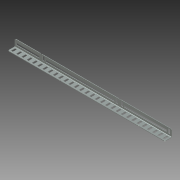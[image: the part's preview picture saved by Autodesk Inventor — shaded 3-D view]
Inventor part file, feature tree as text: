
AUTODESK INVENTOR PART (.ipt)
format: ipt  version: 2013 (Build 170138000, 138)  size: 679,424 bytes
history: native  units: mm (DEFAULTED — no unit token found)
features: other x79, extrude x75, sketch x8, sheet_metal_op x3, pattern_linear x1
ambient origin geometry x8: Origin, YZ Plane, XZ Plane, XY Plane, X Axis, Y Axis, Z Axis, Center Point
bodies: Solid1 (feature_tree)
feature tree (166):
  sheet_metal_op  "Face1"
  sheet_metal_op  "Flange1"
  other  "Corner Chamfer1"
  extrude  "Extrusion1"  Depth=9.779mm
  pattern_linear  "Rectangular Pattern1"  Count1=30 Spacing1=12.7mm
  sketch  "Sketch8"  dims[d25=4.064mm d26=1.905mm d27=1.905mm d28=1.905mm d29=1.905mm d30=1.27mm d31=1.27mm d32=0.635mm d33=2.54mm d34=1.27mm d35=16.51mm d36=90.0deg d37=0.8636mm d38=1.905mm d39=6.35mm d40=45.0deg d41=3.302mm d42=4.064mm d43=4.572mm d45=1.905mm d46=1.905mm d47=0.0mm d48=4.064mm d49=4.572mm d50=3.429mm d51=9.779mm d52=3.048mm d53=4.572mm d54=177.8mm d55=3.048mm d56=4.572mm d58=1.905mm d59=1.905mm d60=0.0mm d61=4.064mm d62=4.064mm d63=4.572mm d64=3.048mm d65=4.064mm d67=3.048mm d68=4.572mm d69=1.27mm d70=0.0mm d71=0.508mm d72=0.508mm d73=13.208mm d74=3.81mm d75=3.048mm d76=0.0mm d77=0.508mm d78=0.508mm d79=3.81mm d80=13.208mm d81=3.302mm d82=25.4mm d83=0.0mm d84=25.4mm d85=0.0mm d86=300.0mm d88=12.7mm d89=0.0mm d90=0.0mm d91=0.0mm d92=0.0mm d93=0.0mm d94=0.0mm d95=0.0mm d96=0.0mm d97=0.0mm d98=0.0mm d99=0.0mm d100=0.0mm d101=0.0mm d102=0.0mm d103=0.0mm d104=0.0mm d105=0.0mm d106=0.0mm d107=0.0mm d108=0.0mm d109=0.0mm d110=0.0mm d111=0.0mm d112=0.0mm d113=0.0mm d114=0.0mm d115=0.0mm d116=0.0mm d117=0.0mm d118=0.0mm d119=0.0mm d120=0.0mm d121=0.0mm d122=0.0mm d123=0.0mm d124=0.0mm d125=0.0mm d126=0.0mm d127=0.0mm d128=0.0mm d129=0.0mm d130=0.0mm d131=0.0mm d132=0.0mm d133=0.0mm d134=0.0mm d135=0.0mm d136=0.0mm d137=0.0mm d138=0.0mm d139=0.0mm d140=0.0mm d141=0.0mm d142=0.0mm d143=0.0mm d144=0.0mm d145=0.0mm d146=0.0mm d147=0.0mm d148=0.0mm d149=0.0mm d150=0.0mm d151=0.0mm d152=0.0mm d153=0.0mm d154=0.0mm d155=0.0mm d156=0.0mm d157=0.0mm d158=0.0mm d159=0.0mm d160=0.0mm d161=0.0mm d162=0.0mm d163=0.0mm d164=0.0mm d165=0.0mm d166=0.0mm d167=0.0mm d168=0.0mm d169=0.0mm d170=0.0mm d171=0.0mm d172=0.0mm d173=0.0mm d174=0.0mm d175=0.0mm d176=0.0mm d177=0.0mm d178=0.0mm d179=0.0mm d180=0.0mm d181=0.0mm d182=0.0mm d183=0.0mm d184=0.0mm d185=0.0mm d186=0.0mm d187=0.0mm d188=0.0mm d189=0.0mm d190=0.0mm d191=0.0mm d192=0.0mm d193=0.0mm d194=0.0mm d195=0.0mm d196=0.0mm d197=0.0mm d198=0.0mm d199=0.0mm d200=0.0mm d201=0.0mm d202=0.0mm d229=1.27mm d230=0.0mm d231=127.0mm d232=1.905mm d233=1.905mm d234=63.179403mm d235=1.905mm d236=1.905mm d237=25.4mm d238=0.0mm d239=25.4mm d240=0.0mm d241=25.4mm d242=0.0mm d243=25.4mm d244=0.0mm d245=25.4mm d246=0.0mm d247=25.4mm d248=0.0mm d249=25.4mm d250=0.0mm d251=25.4mm d252=0.0mm d253=25.4mm d254=0.0mm d255=25.4mm d256=0.0mm d257=25.4mm d258=0.0mm d259=25.4mm d260=0.0mm d261=25.4mm d262=0.0mm d263=25.4mm d264=0.0mm d265=0.0mm d266=0.0mm d267=0.0mm d268=0.0mm d269=0.0mm d270=0.0mm d271=0.0mm d272=0.0mm d273=0.0mm d274=0.0mm d275=0.0mm d276=0.0mm d277=0.0mm d278=0.0mm d279=0.0mm d280=0.0mm d281=0.0mm d282=0.0mm d283=0.0mm d284=0.0mm d285=0.0mm d286=0.0mm d287=0.0mm d288=0.0mm d289=0.0mm d290=0.0mm d291=0.0mm d292=0.0mm]
  sketch  "Sketch1"  dims[d1=4.064mm d2=9.779mm]
  other  "Plate1"
  sketch  "Sketch2"  dims[d3=4.572mm]
  other  "Plate2"
  sheet_metal_op  "Bend1"
  sketch  "Sketch3"  dims[d12=16.51mm]
  sketch  "Sketch4"  dims[d14=1.905mm]
  sketch  "Sketch5"  dims[d15=1.905mm]
  other  "Srf1"
  sketch  "Sketch6"  dims[d16=1.905mm]
  other  "Srf2"
  other  "Srf4"
  other  "Srf6"
  other  "Srf8"
  other  "Srf10"
  other  "Srf12"
  other  "Srf14"
  other  "Srf16"
  other  "Srf18"
  other  "Srf20"
  other  "Srf22"
  other  "Srf24"
  other  "Srf26"
  other  "Srf28"
  other  "Srf30"
  other  "Srf32"
  other  "Srf34"
  other  "Srf36"
  other  "Srf38"
  other  "Srf40"
  other  "Srf42"
  other  "Srf44"
  other  "Srf46"
  other  "Srf48"
  other  "Srf50"
  other  "Srf52"
  other  "Srf54"
  other  "Srf56"
  other  "Srf58"
  other  "Srf60"
  other  "Srf3"
  other  "Srf5"
  other  "Srf7"
  other  "Srf9"
  other  "Srf11"
  other  "Srf13"
  other  "Srf15"
  other  "Srf17"
  other  "Srf19"
  other  "Srf21"
  other  "Srf23"
  other  "Srf25"
  other  "Srf27"
  other  "Srf29"
  other  "Srf31"
  other  "Srf33"
  other  "Srf35"
  other  "Srf37"
  other  "Srf39"
  other  "Srf41"
  other  "Srf43"
  other  "Srf45"
  other  "Srf47"
  other  "Srf49"
  other  "Srf51"
  other  "Srf53"
  other  "Srf55"
  other  "Srf57"
  other  "Srf59"
  sketch  "Sketch7"  dims[d17=1.905mm d18=300.0mm d20=12.7mm d21=10.0mm d23=25.4mm]
  other  "Srf61"
  other  "Srf62"
  other  "Srf63"
  other  "Srf64"
  other  "Srf65"
  other  "Srf66"
  other  "Srf67"
  other  "Srf68"
  other  "Srf69"
  other  "Srf70"
  other  "Srf71"
  other  "Srf72"
  other  "Srf73"
  other  "Srf74"
  other  "Cut1"
  extrude  "ExtrusionSrf1"  Depth=1.905mm
  extrude  "ExtrusionSrf2"  Depth=1.905mm
  other  "Cut2"
  extrude  "ExtrusionSrf61"  Depth=1.905mm
  extrude  "ExtrusionSrf62"  Depth=1.905mm
  extrude  "ExtrusionSrf63"  Depth=1.27mm
  extrude  "ExtrusionSrf64"  Depth=1.27mm
  extrude  "ExtrusionSrf65"  Depth=0.635mm
  extrude  "ExtrusionSrf66"  Depth=2.54mm
  extrude  "ExtrusionSrf67"  Depth=1.27mm
  extrude  "ExtrusionSrf68"  Depth=16.51mm TaperAngle=90.0deg
  extrude  "ExtrusionSrf69"  Depth=1.905mm TaperAngle=45.0deg
  extrude  "ExtrusionSrf70"  Depth=3.302mm
  extrude  "ExtrusionSrf71"  Depth=4.064mm
  extrude  "ExtrusionSrf72"  Depth=4.572mm
  extrude  "ExtrusionSrf73"  Depth=1.905mm
  extrude  "ExtrusionSrf74"  Depth=1.905mm
  extrude  "ExtrusionSrf3"  TaperAngle=0.0deg  [1 undecoded]
  extrude  "ExtrusionSrf4"  Depth=4.064mm
  extrude  "ExtrusionSrf5"  Depth=4.572mm
  extrude  "ExtrusionSrf6"  Depth=3.429mm
  extrude  "ExtrusionSrf7"  Depth=9.779mm
  extrude  "ExtrusionSrf8"  Depth=3.048mm
  extrude  "ExtrusionSrf9"  Depth=4.572mm
  extrude  "ExtrusionSrf10"  Depth=177.8mm
  extrude  "ExtrusionSrf11"  Depth=3.048mm
  extrude  "ExtrusionSrf12"  Depth=4.572mm
  extrude  "ExtrusionSrf13"  Depth=1.905mm
  extrude  "ExtrusionSrf14"  Depth=1.905mm
  extrude  "ExtrusionSrf15"  TaperAngle=0.0deg  [1 undecoded]
  extrude  "ExtrusionSrf16"  Depth=4.064mm
  extrude  "ExtrusionSrf17"  Depth=4.064mm
  extrude  "ExtrusionSrf18"  Depth=4.572mm
  extrude  "ExtrusionSrf19"  Depth=3.048mm
  extrude  "ExtrusionSrf20"  Depth=4.064mm
  extrude  "ExtrusionSrf21"  Depth=3.048mm
  extrude  "ExtrusionSrf22"  Depth=4.572mm
  extrude  "ExtrusionSrf23"  Depth=1.27mm
  extrude  "ExtrusionSrf24"  TaperAngle=0.0deg  [1 undecoded]
  extrude  "ExtrusionSrf25"  Depth=0.508mm
  extrude  "ExtrusionSrf26"  Depth=0.508mm
  extrude  "ExtrusionSrf27"  Depth=13.208mm
  extrude  "ExtrusionSrf28"  Depth=3.81mm
  extrude  "ExtrusionSrf29"  Depth=3.048mm TaperAngle=0.0deg
  extrude  "ExtrusionSrf30"  Depth=0.508mm
  extrude  "ExtrusionSrf31"  Depth=0.508mm
  extrude  "ExtrusionSrf32"  Depth=3.81mm
  extrude  "ExtrusionSrf33"  Depth=13.208mm
  extrude  "ExtrusionSrf34"  Depth=3.302mm
  extrude  "ExtrusionSrf35"  Depth=25.4mm TaperAngle=0.0deg
  extrude  "ExtrusionSrf36"  Depth=25.4mm TaperAngle=0.0deg
  extrude  "ExtrusionSrf37"  Depth=300.0mm
  extrude  "ExtrusionSrf38"  TaperAngle=0.0deg  [1 undecoded]
  extrude  "ExtrusionSrf39"  TaperAngle=0.0deg  [1 undecoded]
  extrude  "ExtrusionSrf40"  TaperAngle=0.0deg  [1 undecoded]
  extrude  "ExtrusionSrf41"  TaperAngle=0.0deg  [1 undecoded]
  extrude  "ExtrusionSrf42"  TaperAngle=0.0deg  [1 undecoded]
  extrude  "ExtrusionSrf43"  TaperAngle=0.0deg  [1 undecoded]
  extrude  "ExtrusionSrf44"  TaperAngle=0.0deg  [1 undecoded]
  extrude  "ExtrusionSrf45"  TaperAngle=0.0deg  [1 undecoded]
  extrude  "ExtrusionSrf46"  TaperAngle=0.0deg  [1 undecoded]
  extrude  "ExtrusionSrf47"  TaperAngle=0.0deg  [1 undecoded]
  extrude  "ExtrusionSrf48"  TaperAngle=0.0deg  [1 undecoded]
  extrude  "ExtrusionSrf49"  TaperAngle=0.0deg  [1 undecoded]
  extrude  "ExtrusionSrf50"  TaperAngle=0.0deg  [1 undecoded]
  extrude  "ExtrusionSrf51"  TaperAngle=0.0deg  [1 undecoded]
  extrude  "ExtrusionSrf52"  TaperAngle=0.0deg  [1 undecoded]
  extrude  "ExtrusionSrf53"  TaperAngle=0.0deg  [1 undecoded]
  extrude  "ExtrusionSrf54"  TaperAngle=0.0deg  [1 undecoded]
  extrude  "ExtrusionSrf55"  TaperAngle=0.0deg  [1 undecoded]
  extrude  "ExtrusionSrf56"  TaperAngle=0.0deg  [1 undecoded]
  extrude  "ExtrusionSrf57"  TaperAngle=0.0deg  [1 undecoded]
  extrude  "ExtrusionSrf58"  TaperAngle=0.0deg  [1 undecoded]
  extrude  "ExtrusionSrf59"  TaperAngle=0.0deg  [1 undecoded]
  extrude  "ExtrusionSrf60"  TaperAngle=0.0deg  [1 undecoded]
note: 26 required parameter values undecoded (feature->parameter linkage not recoverable at this tier; creation-order binding heuristic only, values carry confidence <= 0.55)
